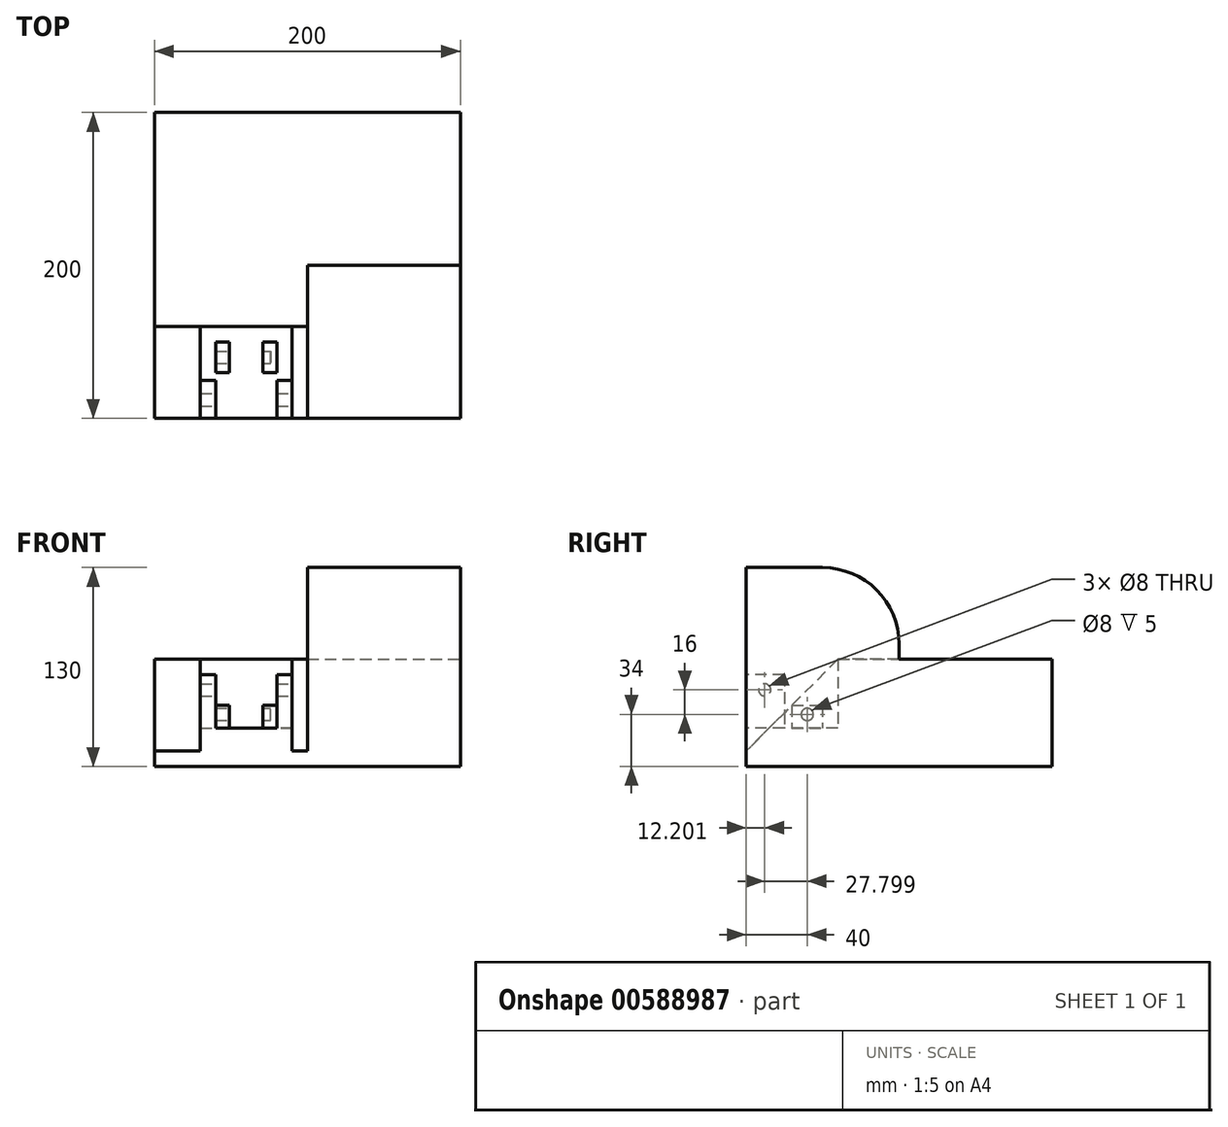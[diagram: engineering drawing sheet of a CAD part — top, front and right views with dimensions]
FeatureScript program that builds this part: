
annotation { "Feature Type Name" : "Feature", "Feature Type Description" : "" }
export const myFeature = defineFeature(function(context is Context, id is Id, definition is map)
    precondition{}
    {
        {
            var Q0;
            Q0=qCreatedBy(makeId("Top.planeOp"),FACE);
            var sketch = newSketch(context, id + "F0", { "sketchPlane" : qUnion([Q0])});
            skLineSegment(sketch, "E0.bottom", {"start": v(100, -100) * mm, "end": v(-100, -100) * mm});
            skLineSegment(sketch, "E0.top", {"start": v(100, 100) * mm, "end": v(-100, 100) * mm});
            skLineSegment(sketch, "E0.left", {"start": v(100, -100) * mm, "end": v(100, 100) * mm});
            skLineSegment(sketch, "E0.right", {"start": v(-100, -100) * mm, "end": v(-100, 100) * mm});
            skPoint(sketch, "E0.middle", {"position": v(0, 0) * mm});
            skLineSegment(sketch, "E1", {"start": v(-70, -40) * mm, "end": v(-70, -100) * mm});
            skLineSegment(sketch, "E2", {"start": v(-70, -40) * mm, "end": v(-10, -40) * mm});
            skLineSegment(sketch, "E3", {"start": v(-10, -40) * mm, "end": v(-10, -100) * mm});
            skLineSegment(sketch, "E4", {"start": v(-80, -100) * mm, "end": v(-70, -100) * mm});
            skLineSegment(sketch, "E5", {"start": v(-10, -100) * mm, "end": v(-10, -100) * mm});
            skLineSegment(sketch, "E6", {"start": v(0, 0) * mm, "end": v(0, -100) * mm});
            skLineSegment(sketch, "E7", {"start": v(0, 0) * mm, "end": v(100, 0) * mm});
            skLineSegment(sketch, "E8.left", {"start": v(-29, -70) * mm, "end": v(-29, -50) * mm});
            skLineSegment(sketch, "E8.right", {"start": v(-51, -70) * mm, "end": v(-51, -50) * mm});
            skPoint(sketch, "E8.middle", {"position": v(-40, -60) * mm});
            skPoint(sketch, "E8.middle.positionSnap0", {"position": v(-40, -40) * mm});
            skPoint(sketch, "E8.centerSnap0", {"position": v(-40, -40) * mm});
            skLineSegment(sketch, "E9.bottom", {"start": v(-20, -70) * mm, "end": v(-29, -70) * mm});
            skLineSegment(sketch, "E9.top", {"start": v(-20, -50) * mm, "end": v(-29, -50) * mm});
            skLineSegment(sketch, "E9.left", {"start": v(-20, -70) * mm, "end": v(-20, -50) * mm});
            skLineSegment(sketch, "E9.right", {"start": v(-60, -70) * mm, "end": v(-60, -50) * mm});
            skPoint(sketch, "E8.top.end.orphan", {"position": v(-51, -41.49) * mm});
            skPoint(sketch, "E10.orphan", {"position": v(-29, -41.49) * mm});
            skLineSegment(sketch, "E11.trimOffspring", {"start": v(-51, -50) * mm, "end": v(-60, -50) * mm});
            skLineSegment(sketch, "E12.trimOffspring", {"start": v(-51, -70) * mm, "end": v(-60, -70) * mm});
            skPoint(sketch, "E13.orphan", {"position": v(-51, -78.51) * mm});
            skPoint(sketch, "E14.orphan", {"position": v(-29, -78.51) * mm});
            skLineSegment(sketch, "E15", {"start": v(-70, -75) * mm, "end": v(-60, -75) * mm});
            skLineSegment(sketch, "E16", {"start": v(-60, -75) * mm, "end": v(-60, -100) * mm});
            skLineSegment(sketch, "E17", {"start": v(-10, -75) * mm, "end": v(-20, -75) * mm});
            skLineSegment(sketch, "E18", {"start": v(-20, -75) * mm, "end": v(-20, -100) * mm});
            skSolve(sketch);
        }
        {
            var Q0;
            {var subQ12=sQuery(id+"F0.wireOp",EDGE,"E0.top");Q0=makeQuery(id+"F0.imprint","IMPRINT",FACE,{"disambiguationData":[TD([[makeQuery(id+"F0.imprint","IMPRINT",EDGE,{"derivedFrom":subQ12}),1.0]])]});}
            extrude(context, id + "F1", {"entities" : qUnion([Q0]), "depth" : 70 * mm, "offsetDistance" : 25 * mm});
        }
        {
            var Q0;
            {var subQ3=sQuery(id+"F0.wireOp",EDGE,"E6");Q0=makeQuery(id+"F0.imprint","IMPRINT",FACE,{"disambiguationData":[TD([[makeQuery(id+"F0.imprint","IMPRINT",EDGE,{"derivedFrom":subQ3}),1.0]])]});}
            extrude(context, id + "F2", {"entities" : qUnion([Q0]), "operationType" : NewBodyOperationType.ADD, "depth" : 130 * mm, "offsetDistance" : 25 * mm});
        }
        {
            var Q0;
            Q0=makeQuery(id+"F2.opExtrude","CAP_EDGE",EDGE,{"disambiguationData":[OSD([sQuery(id+"F0.wireOp",EDGE,"E7")])],"isStart":false});
            fillet(context, id + "F3", {"entities" : qUnion([Q0]), "tangentPropagation" : true, "radius" : 50 * mm, "defaultsChanged" : false, "vertexSettings" : [], "allowEdgeOverflow" : false});
        }
        {
            var Q0;
            {var subQ0=sQuery(id+"F0.wireOp",EDGE,"E0.bottom");Q0=makeQuery(id+"F1.opExtrude","CAP_EDGE",EDGE,{"disambiguationData":[OSD([subQ0]),TDD([makeQuery(id+"F0.imprint","IMPRINT",EDGE,{"disambiguationData":[TD([[makeQuery(id+"F0.imprint","INTERSECT",VERTEX,{"derivedFrom":[subQ0,sQuery(id+"F0.wireOp",EDGE,"E0.right")]}),1.0]])],"derivedFrom":subQ0})])],"isStart":false});}
            var Q1;
            {var subQ0=sQuery(id+"F0.wireOp",EDGE,"E0.bottom");Q1=makeQuery(id+"F1.opExtrude","CAP_EDGE",EDGE,{"disambiguationData":[OSD([subQ0]),TDD([makeQuery(id+"F0.imprint","IMPRINT",EDGE,{"disambiguationData":[TD([[makeQuery(id+"F0.imprint","INTERSECT",VERTEX,{"derivedFrom":[subQ0,sQuery(id+"F0.wireOp",EDGE,"E6")]}),-1.0]])],"derivedFrom":subQ0})])],"isStart":false});}
            var Q2;
            Q2=makeQuery(id+"F1.opExtrude","CAP_EDGE",EDGE,{"disambiguationData":[OSD([sQuery(id+"F0.wireOp",EDGE,"E0.bottom"),sQuery(id+"F0.wireOp",EDGE,"E4")])],"isStart":false});
            chamfer(context, id + "F4", {"entities" : qUnion([Q0, Q1, Q2]), "width" : 60 * mm, "tangentPropagation" : true});
        }
        {
            var Q0;
            {var subQ4=sQuery(id+"F0.wireOp",EDGE,"E15");Q0=makeQuery(id+"F0.imprint","IMPRINT",FACE,{"disambiguationData":[TD([[makeQuery(id+"F0.imprint","IMPRINT",EDGE,{"derivedFrom":subQ4}),-1.0]])]});}
            var Q1;
            {var subQ4=sQuery(id+"F0.wireOp",EDGE,"E17");Q1=makeQuery(id+"F0.imprint","IMPRINT",FACE,{"disambiguationData":[TD([[makeQuery(id+"F0.imprint","IMPRINT",EDGE,{"derivedFrom":subQ4}),1.0]])]});}
            extrude(context, id + "F5", {"entities" : qUnion([Q0, Q1]), "operationType" : NewBodyOperationType.ADD, "depth" : 60 * mm, "offsetDistance" : 25 * mm});
        }
        {
            var Q0;
            {var subQ4=sQuery(id+"F0.wireOp",EDGE,"E2");Q0=makeQuery(id+"F0.imprint","IMPRINT",FACE,{"disambiguationData":[TD([[makeQuery(id+"F0.imprint","IMPRINT",EDGE,{"derivedFrom":subQ4}),-1.0]])]});}
            extrude(context, id + "F6", {"entities" : qUnion([Q0]), "operationType" : NewBodyOperationType.ADD, "depth" : 25 * mm, "offsetDistance" : 25 * mm});
        }
        {
            var Q0;
            Q0=makeQuery(id+"F0.imprint","IMPRINT",FACE,{"disambiguationData":[TD([[makeQuery(id+"F0.imprint","IMPRINT",EDGE,{"derivedFrom":sQuery(id+"F0.wireOp",EDGE,"E8.left")}),-1.0]])]});
            var Q1;
            Q1=makeQuery(id+"F0.imprint","IMPRINT",FACE,{"disambiguationData":[TD([[makeQuery(id+"F0.imprint","IMPRINT",EDGE,{"derivedFrom":sQuery(id+"F0.wireOp",EDGE,"E8.right")}),1.0]])]});
            extrude(context, id + "F7", {"entities" : qUnion([Q0, Q1]), "operationType" : NewBodyOperationType.ADD, "depth" : 40 * mm, "offsetDistance" : 25 * mm});
        }
        {
            var Q0;
            Q0=qCreatedBy(makeId("Right.planeOp"),FACE);
            cPlane(context, id + "F8", {"entities" : qUnion([Q0]), "cplaneType" : CPlaneType.OFFSET, "offset" : 45 * mm, "oppositeDirection" : true, "width" : 150 * mm, "height" : 150 * mm});
        }
        {
            var Q0;
            Q0=qCreatedBy(id+"F8.planeOp",FACE);
            var sketch = newSketch(context, id + "F9", { "sketchPlane" : qUnion([Q0])});
            skCircle(sketch, "E19", {"center": v(-87.8, 50) * mm, "radius": 4 * mm});
            skCircle(sketch, "E20", {"center": v(-60, 34) * mm, "radius": 4 * mm});
            skLineSegment(sketch, "E21.0.0", {"start": v(-50, 25) * mm, "end": v(-70, 25) * mm});
            skLineSegment(sketch, "E21.0.1", {"start": v(-70, 25) * mm, "end": v(-70, 40) * mm});
            skLineSegment(sketch, "E21.0.2", {"start": v(-70, 40) * mm, "end": v(-50, 40) * mm});
            skLineSegment(sketch, "E21.0.3", {"start": v(-50, 40) * mm, "end": v(-50, 25) * mm});
            skSolve(sketch);
        }
        {
            var Q0;
            Q0=makeQuery(id+"F9.imprint","IMPRINT",FACE,{"disambiguationData":[TD([[makeQuery(id+"F9.imprint","IMPRINT",EDGE,{"derivedFrom":sQuery(id+"F9.wireOp",EDGE,"E20")}),1.0]])]});
            extrude(context, id + "F10", {"entities" : qUnion([Q0]), "operationType" : NewBodyOperationType.REMOVE, "endBound" : BoundingType.SYMMETRIC, "oppositeDirection" : true, "depth" : 42 * mm, "offsetDistance" : 25 * mm});
        }
        {
            var Q0;
            Q0=makeQuery(id+"F9.imprint","IMPRINT",FACE,{"disambiguationData":[TD([[makeQuery(id+"F9.imprint","IMPRINT",EDGE,{"derivedFrom":sQuery(id+"F9.wireOp",EDGE,"E19")}),1.0]])]});
            extrude(context, id + "F11", {"entities" : qUnion([Q0]), "operationType" : NewBodyOperationType.REMOVE, "endBound" : BoundingType.SYMMETRIC, "oppositeDirection" : true, "depth" : 72.8 * mm, "offsetDistance" : 25 * mm});
        }
    });
